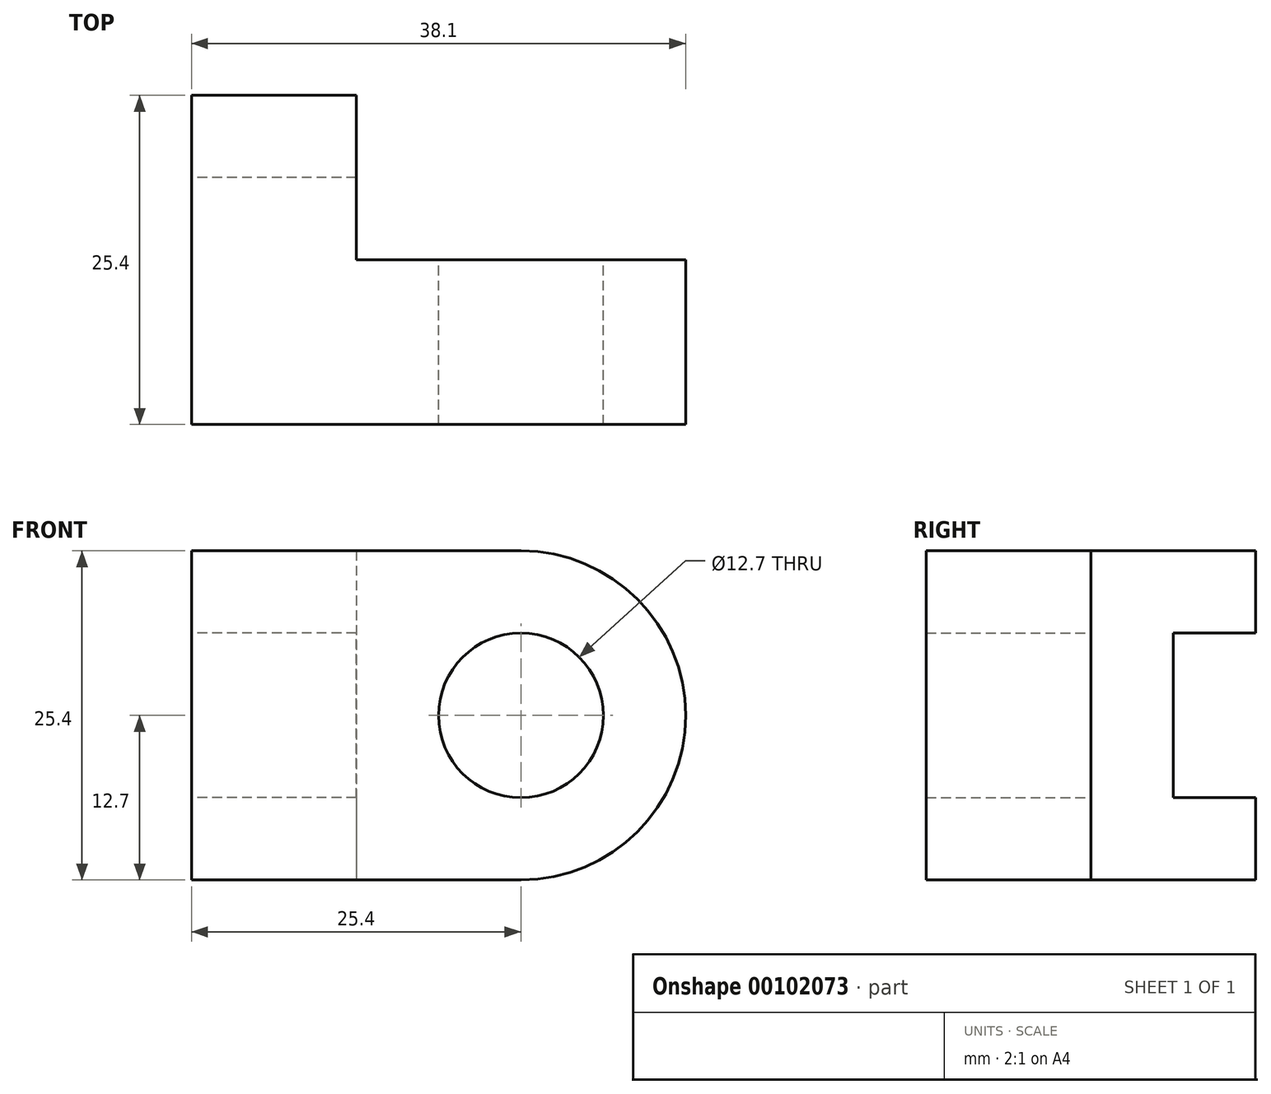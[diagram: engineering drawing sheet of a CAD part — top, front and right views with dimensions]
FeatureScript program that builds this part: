
annotation { "Feature Type Name" : "Feature", "Feature Type Description" : "" }
export const myFeature = defineFeature(function(context is Context, id is Id, definition is map)
    precondition{}
    {
        {
            var Q0;
            Q0=qCreatedBy(makeId("Front.planeOp"),FACE);
            var sketch = newSketch(context, id + "F0", { "sketchPlane" : qUnion([Q0])});
            skLineSegment(sketch, "E0", {"start": v(0, 0) * mm, "end": v(0, 25.4) * mm});
            skLineSegment(sketch, "E1", {"start": v(0, 25.4) * mm, "end": v(25.4, 25.4) * mm});
            skLineSegment(sketch, "E2", {"start": v(0, 0) * mm, "end": v(25.4, 0) * mm});
            skArc(sketch, "E3", {"start": v(25.4, 25.4) * mm, "mid": v(38.1, 12.7) * mm, "end": v(25.4, 0) * mm});
            skSolve(sketch);
        }
        {
            var Q0;
            Q0 = qSketchRegion(id + "F0", true);
            extrude(context, id + "F1", {"entities" : qUnion([Q0]), "depth" : 25.4 * mm});
        }
        {
            var Q0;
            Q0=qCreatedBy(makeId("Front.planeOp"),FACE);
            var sketch = newSketch(context, id + "F2", { "sketchPlane" : qUnion([Q0])});
            skLineSegment(sketch, "E4", {"start": v(12.7, 25.4) * mm, "end": v(12.7, 0) * mm});
            skLineSegment(sketch, "E5", {"start": v(12.7, 0) * mm, "end": v(25.4, 0) * mm});
            skLineSegment(sketch, "E6", {"start": v(12.7, 25.4) * mm, "end": v(25.4, 25.4) * mm});
            skArc(sketch, "E7", {"start": v(25.4, 25.4) * mm, "mid": v(38.1, 12.7) * mm, "end": v(25.4, 0) * mm});
            skSolve(sketch);
        }
        {
            var Q0;
            Q0 = qSketchRegion(id + "F2", true);
            extrude(context, id + "F3", {"entities" : qUnion([Q0]), "operationType" : NewBodyOperationType.REMOVE, "depth" : 12.7 * mm});
        }
        {
            var Q0;
            Q0=qCreatedBy(makeId("Front.planeOp"),FACE);
            var sketch = newSketch(context, id + "F4", { "sketchPlane" : qUnion([Q0])});
            skCircle(sketch, "E8", {"center": v(25.4, 12.7) * mm, "radius": 6.35 * mm});
            skSolve(sketch);
        }
        {
            var Q0;
            Q0 = qSketchRegion(id + "F4", true);
            extrude(context, id + "F5", {"entities" : qUnion([Q0]), "operationType" : NewBodyOperationType.REMOVE, "depth" : 25.4 * mm});
        }
        {
            var Q0;
            Q0=qCreatedBy(makeId("Right.planeOp"),FACE);
            var sketch = newSketch(context, id + "F6", { "sketchPlane" : qUnion([Q0])});
            skLineSegment(sketch, "E9.bottom", {"start": v(0, 19.05) * mm, "end": v(-6.35, 19.05) * mm});
            skLineSegment(sketch, "E9.top", {"start": v(0, 6.35) * mm, "end": v(-6.35, 6.35) * mm});
            skLineSegment(sketch, "E9.left", {"start": v(0, 19.05) * mm, "end": v(0, 6.35) * mm});
            skLineSegment(sketch, "E9.right", {"start": v(-6.35, 19.05) * mm, "end": v(-6.35, 6.35) * mm});
            skSolve(sketch);
        }
        {
            var Q0;
            Q0 = qSketchRegion(id + "F6", true);
            extrude(context, id + "F7", {"entities" : qUnion([Q0]), "operationType" : NewBodyOperationType.REMOVE, "depth" : 25.4 * mm});
        }
    });
